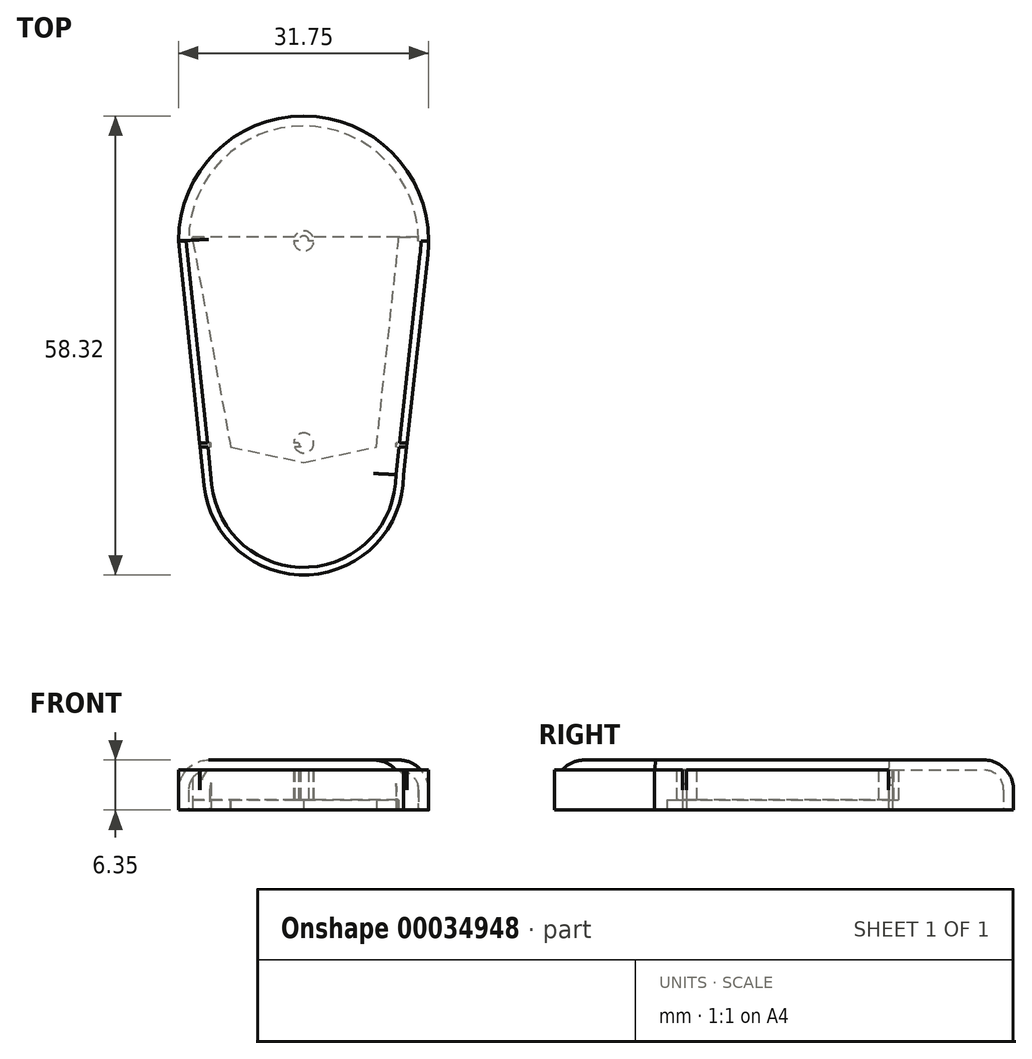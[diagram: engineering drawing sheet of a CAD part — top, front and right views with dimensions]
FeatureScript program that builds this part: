
annotation { "Feature Type Name" : "Feature", "Feature Type Description" : "" }
export const myFeature = defineFeature(function(context is Context, id is Id, definition is map)
    precondition{}
    {
        {
            var Q0;
            Q0=qCreatedBy(makeId("Top.planeOp"),FACE);
            var sketch = newSketch(context, id + "F0", { "sketchPlane" : qUnion([Q0])});
            skCircle(sketch, "E0", {"center": v(-0.02, 15.04) * mm, "radius": 15.88 * mm});
            skCircle(sketch, "E1", {"center": v(-0.02, -14.7) * mm, "radius": 12.7 * mm});
            skLineSegment(sketch, "E2", {"start": v(12.68, -14.7) * mm, "end": v(15.95, 15.04) * mm});
            skLineSegment(sketch, "E3", {"start": v(-15.9, 15.04) * mm, "end": v(-12.65, -16.03) * mm});
            skSolve(sketch);
        }
        {
            var Q0;
            {var subQ1=sQuery(id+"F0.wireOp",EDGE,"E0");var subQ4=makeQuery(id+"F0.imprint","INTERSECT",VERTEX,{"derivedFrom":[subQ1,sQuery(id+"F0.wireOp",EDGE,"E2")]});Q0=makeQuery(id+"F0.imprint","IMPRINT",FACE,{"disambiguationData":[TD([[makeQuery(id+"F0.imprint","IMPRINT",EDGE,{"disambiguationData":[TD([[subQ4,1.0]])],"derivedFrom":subQ1}),1.0]])]});}
            var Q1;
            {var subQ1=sQuery(id+"F0.wireOp",EDGE,"E0");var subQ5=sQuery(id+"F0.wireOp",EDGE,"E2");var subQ6=makeQuery(id+"F0.imprint","INTERSECT",VERTEX,{"derivedFrom":[subQ1,subQ5]});Q1=makeQuery(id+"F0.imprint","IMPRINT",FACE,{"disambiguationData":[TD([[makeQuery(id+"F0.imprint","IMPRINT",EDGE,{"disambiguationData":[TD([[subQ6,1.0]])],"derivedFrom":subQ1}),-1.0]])]});}
            var Q2;
            {var subQ0=sQuery(id+"F0.wireOp",EDGE,"E1");var subQ2=makeQuery(id+"F0.imprint","INTERSECT",VERTEX,{"derivedFrom":[subQ0,sQuery(id+"F0.wireOp",EDGE,"E2")]});Q2=makeQuery(id+"F0.imprint","IMPRINT",FACE,{"disambiguationData":[TD([[makeQuery(id+"F0.imprint","IMPRINT",EDGE,{"disambiguationData":[TD([[subQ2,-1.0]])],"derivedFrom":subQ0}),1.0]])]});}
            extrude(context, id + "F1", {"entities" : qUnion([Q0, Q1, Q2]), "depth" : 6.35 * mm});
        }
        {
            var Q0;
            Q0=makeQuery(id+"F1.opExtrude","CAP_EDGE",EDGE,{"disambiguationData":[OSD([sQuery(id+"F0.wireOp",EDGE,"E1")])],"isStart":false});
            var Q1;
            Q1=makeQuery(id+"F1.opExtrude","CAP_EDGE",EDGE,{"disambiguationData":[OSD([sQuery(id+"F0.wireOp",EDGE,"E2")])],"isStart":false});
            var Q2;
            Q2=makeQuery(id+"F1.opExtrude","CAP_EDGE",EDGE,{"disambiguationData":[OSD([sQuery(id+"F0.wireOp",EDGE,"E0")])],"isStart":false});
            var Q3;
            Q3=makeQuery(id+"F1.opExtrude","CAP_EDGE",EDGE,{"disambiguationData":[OSD([sQuery(id+"F0.wireOp",EDGE,"E3")])],"isStart":false});
            fillet(context, id + "F2", {"entities" : qUnion([Q0, Q1, Q2, Q3]), "radius" : 3.8 * mm, "tangentPropagation" : true, "allowEdgeOverflow" : false});
        }
        {
            var Q0;
            Q0=makeQuery(id+"F1.opExtrude","CAP_FACE",FACE,{"disambiguationData":[OSD([sQuery(id+"F0.wireOp",EDGE,"E0"),sQuery(id+"F0.wireOp",EDGE,"E1"),sQuery(id+"F0.wireOp",EDGE,"E2"),sQuery(id+"F0.wireOp",EDGE,"E3")])],"isStart":true});
            var sketch = newSketch(context, id + "F3", { "sketchPlane" : qUnion([Q0])});
            skLineSegment(sketch, "E4", {"start": v(13.13, 10.64) * mm, "end": v(-13.21, 10.64) * mm});
            skLineSegment(sketch, "E5", {"start": v(13.07, 11.15) * mm, "end": v(-13.16, 11.15) * mm});
            skLineSegment(sketch, "E6", {"start": v(16, -15.54) * mm, "end": v(-15.95, -15.54) * mm});
            skLineSegment(sketch, "E7", {"start": v(15.95, -15.04) * mm, "end": v(-15.9, -15.04) * mm});
            skCircle(sketch, "E8", {"center": v(0, 10.64) * mm, "radius": 0.64 * mm});
            skCircle(sketch, "E9", {"center": v(0, 10.64) * mm, "radius": 1.27 * mm});
            skCircle(sketch, "E10", {"center": v(0, -15.04) * mm, "radius": 1.27 * mm});
            skCircle(sketch, "E11", {"center": v(0, -15.04) * mm, "radius": 0.64 * mm});
            skLineSegment(sketch, "E12", {"start": v(11.7, 11.15) * mm, "end": v(11.7, 10.64) * mm});
            skLineSegment(sketch, "E13", {"start": v(-11.76, 11.15) * mm, "end": v(-11.76, 10.64) * mm});
            skLineSegment(sketch, "E14", {"start": v(14.52, -15.04) * mm, "end": v(14.52, -15.54) * mm});
            skLineSegment(sketch, "E15", {"start": v(-14.1, -15.04) * mm, "end": v(-14.1, -15.54) * mm});
            skSolve(sketch);
        }
        {
            var Q0;
            Q0=makeQuery(id+"F1.opExtrude","CAP_FACE",FACE,{"disambiguationData":[OSD([sQuery(id+"F0.wireOp",EDGE,"E0"),sQuery(id+"F0.wireOp",EDGE,"E1"),sQuery(id+"F0.wireOp",EDGE,"E2"),sQuery(id+"F0.wireOp",EDGE,"E3")])],"isStart":true});
            shell(context, id + "F4", {"entities" : qUnion([Q0]), "thickness" : 1.27 * mm});
        }
        {
            var Q0;
            {var subQ0=sQuery(id+"F3.wireOp",EDGE,"E12");Q0=makeQuery(id+"F3.imprint","IMPRINT",FACE,{"disambiguationData":[TD([[makeQuery(id+"F3.imprint","IMPRINT",EDGE,{"derivedFrom":subQ0}),-1.0]])]});}
            var Q1;
            {var subQ0=sQuery(id+"F3.wireOp",EDGE,"E9");var subQ1=sQuery(id+"F3.wireOp",EDGE,"E4");var subQ3=makeQuery(id+"F3.imprint","INTERSECT",VERTEX,{"disambiguationData":[OD(0.0)],"derivedFrom":[subQ1,subQ0]});Q1=makeQuery(id+"F3.imprint","IMPRINT",FACE,{"disambiguationData":[TD([[makeQuery(id+"F3.imprint","IMPRINT",EDGE,{"disambiguationData":[TD([[subQ3,-1.0]])],"derivedFrom":subQ1}),1.0]])]});}
            var Q2;
            {var subQ0=sQuery(id+"F3.wireOp",EDGE,"E9");var subQ3=sQuery(id+"F3.wireOp",EDGE,"E4");var subQ4=makeQuery(id+"F3.imprint","INTERSECT",VERTEX,{"disambiguationData":[OD(0.0)],"derivedFrom":[subQ3,subQ0]});Q2=makeQuery(id+"F3.imprint","IMPRINT",FACE,{"disambiguationData":[TD([[makeQuery(id+"F3.imprint","IMPRINT",EDGE,{"disambiguationData":[TD([[subQ4,-1.0]])],"derivedFrom":subQ3}),-1.0]])]});}
            var Q3;
            {var subQ0=sQuery(id+"F3.wireOp",EDGE,"E8");var subQ3=sQuery(id+"F3.wireOp",EDGE,"E4");var subQ4=makeQuery(id+"F3.imprint","INTERSECT",VERTEX,{"disambiguationData":[OD(1.0)],"derivedFrom":[subQ3,subQ0]});Q3=makeQuery(id+"F3.imprint","IMPRINT",FACE,{"disambiguationData":[TD([[makeQuery(id+"F3.imprint","IMPRINT",EDGE,{"disambiguationData":[TD([[subQ4,-1.0]])],"derivedFrom":subQ3}),-1.0]])]});}
            var Q4;
            {var subQ0=sQuery(id+"F3.wireOp",EDGE,"E9");var subQ1=sQuery(id+"F3.wireOp",EDGE,"E5");var subQ3=makeQuery(id+"F3.imprint","INTERSECT",VERTEX,{"disambiguationData":[OD(0.0)],"derivedFrom":[subQ1,subQ0]});Q4=makeQuery(id+"F3.imprint","IMPRINT",FACE,{"disambiguationData":[TD([[makeQuery(id+"F3.imprint","IMPRINT",EDGE,{"disambiguationData":[TD([[subQ3,-1.0]])],"derivedFrom":subQ1}),-1.0]])]});}
            var Q5;
            {var subQ0=sQuery(id+"F3.wireOp",EDGE,"E13");Q5=makeQuery(id+"F3.imprint","IMPRINT",FACE,{"disambiguationData":[TD([[makeQuery(id+"F3.imprint","IMPRINT",EDGE,{"derivedFrom":subQ0}),1.0]])]});}
            var Q6;
            {var subQ0=sQuery(id+"F3.wireOp",EDGE,"E14");Q6=makeQuery(id+"F3.imprint","IMPRINT",FACE,{"disambiguationData":[TD([[makeQuery(id+"F3.imprint","IMPRINT",EDGE,{"derivedFrom":subQ0}),-1.0]])]});}
            var Q7;
            {var subQ1=sQuery(id+"F3.wireOp",EDGE,"E6");var subQ4=sQuery(id+"F3.wireOp",EDGE,"E10");var subQ6=makeQuery(id+"F3.imprint","INTERSECT",VERTEX,{"disambiguationData":[OD(0.0)],"derivedFrom":[subQ1,subQ4]});Q7=makeQuery(id+"F3.imprint","IMPRINT",FACE,{"disambiguationData":[TD([[makeQuery(id+"F3.imprint","IMPRINT",EDGE,{"disambiguationData":[TD([[subQ6,-1.0]])],"derivedFrom":subQ1}),1.0]])]});}
            var Q8;
            {var subQ3=sQuery(id+"F3.wireOp",EDGE,"E6");var subQ5=sQuery(id+"F3.wireOp",EDGE,"E10");var subQ7=makeQuery(id+"F3.imprint","INTERSECT",VERTEX,{"disambiguationData":[OD(0.0)],"derivedFrom":[subQ3,subQ5]});Q8=makeQuery(id+"F3.imprint","IMPRINT",FACE,{"disambiguationData":[TD([[makeQuery(id+"F3.imprint","IMPRINT",EDGE,{"disambiguationData":[TD([[subQ7,-1.0]])],"derivedFrom":subQ3}),-1.0]])]});}
            var Q9;
            {var subQ0=sQuery(id+"F3.wireOp",EDGE,"E11");var subQ3=sQuery(id+"F3.wireOp",EDGE,"E6");var subQ4=makeQuery(id+"F3.imprint","INTERSECT",VERTEX,{"disambiguationData":[OD(1.0)],"derivedFrom":[subQ3,subQ0]});Q9=makeQuery(id+"F3.imprint","IMPRINT",FACE,{"disambiguationData":[TD([[makeQuery(id+"F3.imprint","IMPRINT",EDGE,{"disambiguationData":[TD([[subQ4,-1.0]])],"derivedFrom":subQ3}),-1.0]])]});}
            var Q10;
            {var subQ1=sQuery(id+"F3.wireOp",EDGE,"E7");var subQ4=sQuery(id+"F3.wireOp",EDGE,"E10");var subQ6=makeQuery(id+"F3.imprint","INTERSECT",VERTEX,{"disambiguationData":[OD(0.0)],"derivedFrom":[subQ1,subQ4]});Q10=makeQuery(id+"F3.imprint","IMPRINT",FACE,{"disambiguationData":[TD([[makeQuery(id+"F3.imprint","IMPRINT",EDGE,{"disambiguationData":[TD([[subQ6,-1.0]])],"derivedFrom":subQ1}),-1.0]])]});}
            var Q11;
            {var subQ0=sQuery(id+"F3.wireOp",EDGE,"E15");Q11=makeQuery(id+"F3.imprint","IMPRINT",FACE,{"disambiguationData":[TD([[makeQuery(id+"F3.imprint","IMPRINT",EDGE,{"derivedFrom":subQ0}),1.0]])]});}
            var Q12;
            Q12=makeQuery(id+"F4.opShell","OFFSET_FACE",FACE,{"disambiguationData":[OSD([sQuery(id+"F0.wireOp",EDGE,"E0"),sQuery(id+"F0.wireOp",EDGE,"E1"),sQuery(id+"F0.wireOp",EDGE,"E2"),sQuery(id+"F0.wireOp",EDGE,"E3")])]});
            extrude(context, id + "F5", {"entities" : qUnion([Q0, Q1, Q2, Q3, Q4, Q5, Q6, Q7, Q8, Q9, Q10, Q11]), "operationType" : NewBodyOperationType.ADD, "endBound" : BoundingType.UP_TO_SURFACE, "oppositeDirection" : true, "endBoundEntityFace" : qUnion([Q12]), "depth" : 25.4 * mm});
        }
        {
            var Q0;
            {Q0=qUnion([makeQuery(id+"F5.opExtrude","CAP_FACE",FACE,{"disambiguationData":[OSD([sQuery(id+"F3.wireOp",EDGE,"E4"),sQuery(id+"F3.wireOp",EDGE,"E5"),sQuery(id+"F3.wireOp",EDGE,"E8"),sQuery(id+"F3.wireOp",EDGE,"E9"),sQuery(id+"F3.wireOp",EDGE,"E12"),sQuery(id+"F3.wireOp",EDGE,"E13")])],"isStart":true}),makeQuery(id+"F1.opExtrude","CAP_FACE",FACE,{"disambiguationData":[OSD([sQuery(id+"F0.wireOp",EDGE,"E0"),sQuery(id+"F0.wireOp",EDGE,"E1"),sQuery(id+"F0.wireOp",EDGE,"E2"),sQuery(id+"F0.wireOp",EDGE,"E3")])],"isStart":true}),makeQuery(id+"F5.opExtrude","CAP_FACE",FACE,{"disambiguationData":[OSD([sQuery(id+"F3.wireOp",EDGE,"E6"),sQuery(id+"F3.wireOp",EDGE,"E7"),sQuery(id+"F3.wireOp",EDGE,"E10"),sQuery(id+"F3.wireOp",EDGE,"E11"),sQuery(id+"F3.wireOp",EDGE,"E14"),sQuery(id+"F3.wireOp",EDGE,"E15")])],"isStart":true})]);}
            var sketch = newSketch(context, id + "F6", { "sketchPlane" : qUnion([Q0])});
            skLineSegment(sketch, "E16", {"start": v(9.24, 11.15) * mm, "end": v(12.04, -15.04) * mm});
            skLineSegment(sketch, "E17", {"start": v(12.04, -15.04) * mm, "end": v(12.03, -15.54) * mm});
            skLineSegment(sketch, "E18", {"start": v(12.03, -15.54) * mm, "end": v(0, -18.41) * mm});
            skLineSegment(sketch, "E19", {"start": v(0, -18.41) * mm, "end": v(-14.1, -15.54) * mm});
            skLineSegment(sketch, "E20", {"start": v(-14.1, -15.54) * mm, "end": v(-14.1, -15.04) * mm});
            skLineSegment(sketch, "E21", {"start": v(-14.1, -15.04) * mm, "end": v(-9.38, 10.64) * mm});
            skLineSegment(sketch, "E22", {"start": v(-9.38, 10.64) * mm, "end": v(-9.33, 11.15) * mm});
            skLineSegment(sketch, "E23", {"start": v(-9.33, 11.15) * mm, "end": v(0, 13.1) * mm});
            skLineSegment(sketch, "E24", {"start": v(0, 13.1) * mm, "end": v(9.24, 11.15) * mm});
            skSolve(sketch);
        }
        {
            var Q0;
            Q0=makeQuery(id+"F6.imprint","IMPRINT",FACE,{"disambiguationData":[TD([[makeQuery(id+"F6.imprint","IMPRINT",EDGE,{"derivedFrom":sQuery(id+"F6.wireOp",EDGE,"E22")}),-1.0]])]});
            var Q1;
            Q1=makeQuery(id+"F6.imprint","IMPRINT",FACE,{"disambiguationData":[TD([[makeQuery(id+"F6.imprint","IMPRINT",EDGE,{"derivedFrom":sQuery(id+"F6.wireOp",EDGE,"E17")}),-1.0]])]});
            extrude(context, id + "F7", {"entities" : qUnion([Q0, Q1]), "operationType" : NewBodyOperationType.REMOVE, "oppositeDirection" : true, "depth" : 1.27 * mm});
        }
    });
